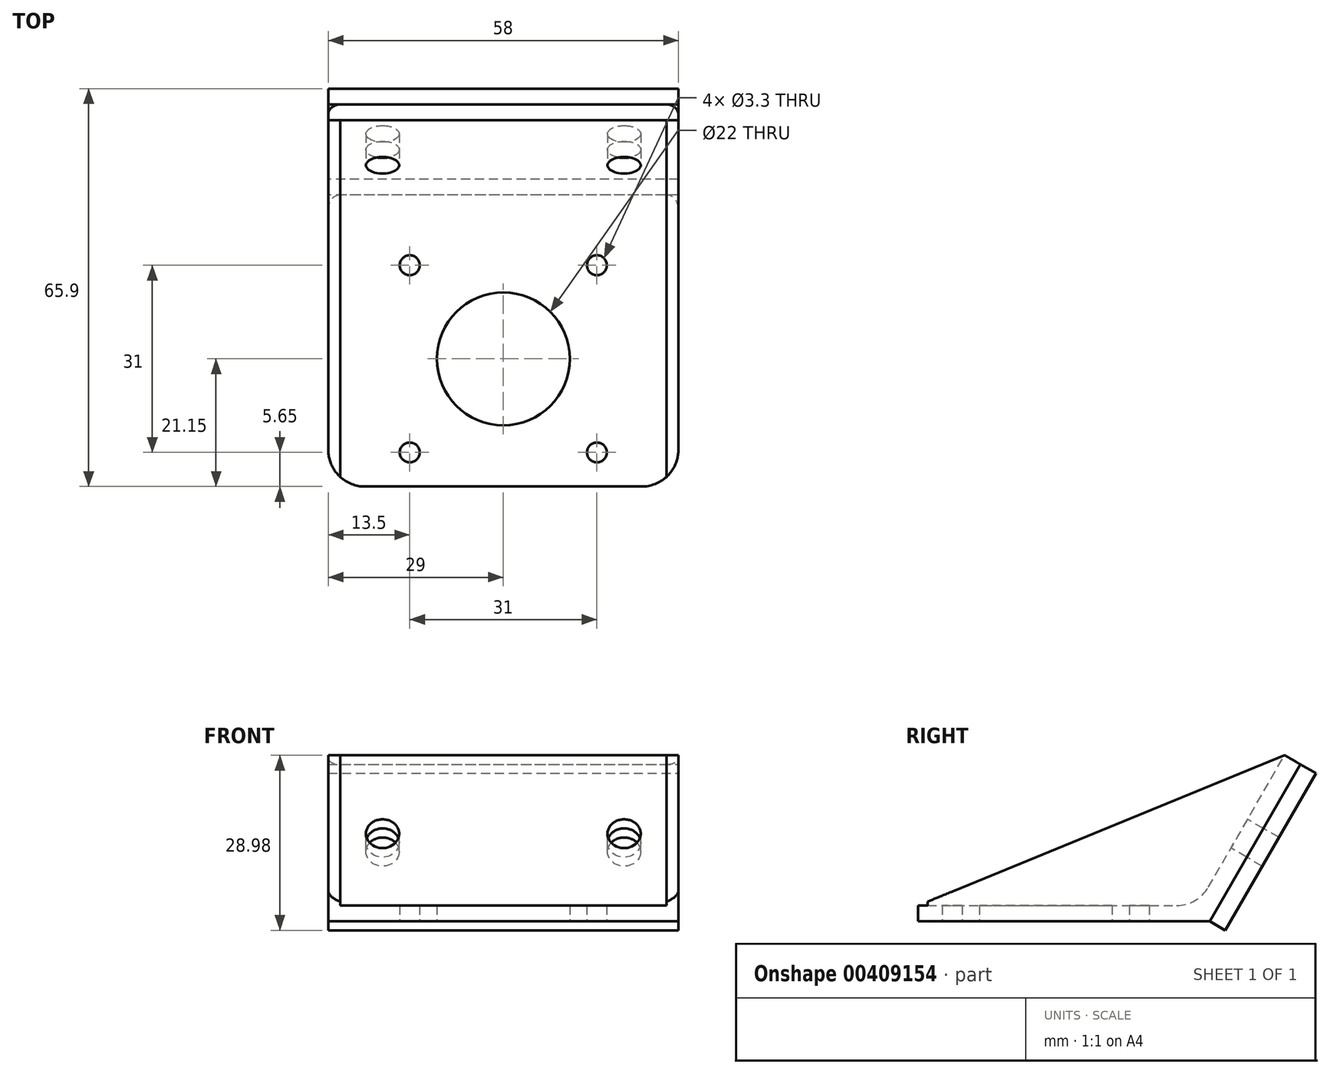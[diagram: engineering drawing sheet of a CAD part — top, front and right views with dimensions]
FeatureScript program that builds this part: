
annotation { "Feature Type Name" : "Feature", "Feature Type Description" : "" }
export const myFeature = defineFeature(function(context is Context, id is Id, definition is map)
    precondition{}
    {
        {
            var Q0;
            Q0=qCreatedBy(makeId("Top.planeOp"),FACE);
            var sketch = newSketch(context, id + "F0", { "sketchPlane" : qUnion([Q0])});
            skLineSegment(sketch, "E0.bottom", {"start": v(-21.15, 21.15) * mm, "end": v(21.15, 21.15) * mm, "construction": true});
            skLineSegment(sketch, "E0.top", {"start": v(-21.15, -21.15) * mm, "end": v(21.15, -21.15) * mm, "construction": true});
            skLineSegment(sketch, "E0.left", {"start": v(-21.15, 21.15) * mm, "end": v(-21.15, -21.15) * mm, "construction": true});
            skLineSegment(sketch, "E0.right", {"start": v(21.15, 21.15) * mm, "end": v(21.15, -21.15) * mm, "construction": true});
            skPoint(sketch, "E0.middle", {"position": v(0, 0) * mm});
            skLineSegment(sketch, "E1.bottom", {"start": v(15.5, -15.5) * mm, "end": v(-15.5, -15.5) * mm, "construction": true});
            skLineSegment(sketch, "E1.top", {"start": v(15.5, 15.5) * mm, "end": v(-15.5, 15.5) * mm, "construction": true});
            skLineSegment(sketch, "E1.left", {"start": v(15.5, -15.5) * mm, "end": v(15.5, 15.5) * mm, "construction": true});
            skLineSegment(sketch, "E1.right", {"start": v(-15.5, -15.5) * mm, "end": v(-15.5, 15.5) * mm, "construction": true});
            skCircle(sketch, "E2", {"center": v(-15.5, 15.5) * mm, "radius": 1.65 * mm});
            skCircle(sketch, "E3", {"center": v(15.5, 15.5) * mm, "radius": 1.65 * mm});
            skCircle(sketch, "E4", {"center": v(-15.5, -15.5) * mm, "radius": 1.65 * mm});
            skCircle(sketch, "E5", {"center": v(15.5, -15.5) * mm, "radius": 1.65 * mm});
            skCircle(sketch, "E6", {"center": v(0, 0) * mm, "radius": 11 * mm});
            skPoint(sketch, "E7.startSnap0", {"position": v(-21.15, 0) * mm});
            skLineSegment(sketch, "E8", {"start": v(0, 21.15) * mm, "end": v(0, -21.15) * mm, "construction": true});
            skLineSegment(sketch, "E9.bottom", {"start": v(29, -21.15) * mm, "end": v(-29, -21.15) * mm});
            skLineSegment(sketch, "E9.top", {"start": v(29, 27.15) * mm, "end": v(-29, 27.15) * mm});
            skLineSegment(sketch, "E9.left", {"start": v(29, -21.15) * mm, "end": v(29, 27.15) * mm});
            skLineSegment(sketch, "E9.right", {"start": v(-29, -21.15) * mm, "end": v(-29, 27.15) * mm});
            skPoint(sketch, "E9.middle", {"position": v(0, 3) * mm});
            skSolve(sketch);
        }
        {
            var Q0;
            Q0=makeQuery(id+"F0.imprint","IMPRINT",FACE,{"disambiguationData":[TD([[makeQuery(id+"F0.imprint","IMPRINT",EDGE,{"derivedFrom":sQuery(id+"F0.wireOp",EDGE,"E2")}),-1.0]])]});
            extrude(context, id + "F1", {"entities" : qUnion([Q0]), "depth" : 2.6 * mm, "offsetDistance" : 25 * mm});
        }
        {
            var Q0;
            Q0=makeQuery(id+"F1.opExtrude","SWEPT_FACE",FACE,{"disambiguationData":[OSD([sQuery(id+"F0.wireOp",EDGE,"E9.top")])]});
            var sketch = newSketch(context, id + "F2", { "sketchPlane" : qUnion([Q0])});
            skLineSegment(sketch, "E10.bottom", {"start": v(29, 0) * mm, "end": v(-29, 0) * mm});
            skLineSegment(sketch, "E10.top", {"start": v(29, 30) * mm, "end": v(-29, 30) * mm});
            skLineSegment(sketch, "E10.left", {"start": v(29, 0) * mm, "end": v(29, 30) * mm});
            skLineSegment(sketch, "E10.right", {"start": v(-29, 0) * mm, "end": v(-29, 30) * mm});
            skPoint(sketch, "E10.middle", {"position": v(0, 15) * mm});
            skCircle(sketch, "E11", {"center": v(20, 15) * mm, "radius": 2.75 * mm});
            skLineSegment(sketch, "E12", {"start": v(29, 15) * mm, "end": v(-29, 15) * mm, "construction": true});
            skCircle(sketch, "E13.MirrorC", {"center": v(-20, 15) * mm, "radius": 2.75 * mm});
            skCircle(sketch, "E14", {"center": v(0, 15) * mm, "radius": 2.75 * mm, "construction": true});
            skSolve(sketch);
        }
        {
            var Q0;
            {var subQ2=sQuery(id+"F2.wireOp",EDGE,"E10.top");Q0=makeQuery(id+"F2.imprint","IMPRINT",FACE,{"disambiguationData":[TD([[makeQuery(id+"F2.imprint","IMPRINT",EDGE,{"derivedFrom":subQ2}),1.0]])]});}
            var Q1;
            {var subQ0=sQuery(id+"F2.wireOp",EDGE,"E10.bottom");Q1=makeQuery(id+"F2.imprint","IMPRINT",FACE,{"disambiguationData":[TD([[makeQuery(id+"F2.imprint","IMPRINT",EDGE,{"derivedFrom":subQ0}),1.0]])]});}
            extrude(context, id + "F3", {"entities" : qUnion([Q0, Q1]), "depth" : 3 * mm, "offsetDistance" : 25 * mm});
        }
        {
            var Q0;
            Q0=makeQuery(id+"F3.opExtrude","SWEPT_BODY",BODY,{"disambiguationData":[OSD([sQuery(id+"F2.wireOp",EDGE,"E10.bottom"),sQuery(id+"F2.wireOp",EDGE,"E10.top"),sQuery(id+"F2.wireOp",EDGE,"E10.left"),sQuery(id+"F2.wireOp",EDGE,"E10.right"),sQuery(id+"F2.wireOp",EDGE,"E11"),sQuery(id+"F2.wireOp",EDGE,"E13.MirrorC")])]});
            var Q1;
            Q1=makeQuery(id+"F3.opExtrude","CAP_EDGE",EDGE,{"disambiguationData":[OSD([sQuery(id+"F2.wireOp",EDGE,"E10.bottom")])],"isStart":false});
            transform(context, id + "F4", {"entities" : qUnion([Q0]), "transformType" : TransformType.ROTATION, "transformAxis" : qUnion([Q1]), "angle" : 30 * degree, "makeCopy" : false});
        }
        {
            var Q0;
            Q0=makeQuery(id+"F3.opExtrude","SWEPT_BODY",BODY,{"disambiguationData":[OSD([sQuery(id+"F2.wireOp",EDGE,"E10.bottom"),sQuery(id+"F2.wireOp",EDGE,"E10.top"),sQuery(id+"F2.wireOp",EDGE,"E10.left"),sQuery(id+"F2.wireOp",EDGE,"E10.right"),sQuery(id+"F2.wireOp",EDGE,"E11"),sQuery(id+"F2.wireOp",EDGE,"E13.MirrorC")])]});
            var Q1;
            Q1=makeQuery(id+"F3.opExtrude","CAP_VERTEX",VERTEX,{"disambiguationData":[OSD([sQuery(id+"F2.wireOp",EDGE,"E10.bottom"),sQuery(id+"F2.wireOp",EDGE,"E10.left")])],"isStart":false});
            var Q2;
            Q2=makeQuery(id+"F1.opExtrude","CAP_VERTEX",VERTEX,{"disambiguationData":[OSD([sQuery(id+"F0.wireOp",EDGE,"E9.top"),sQuery(id+"F0.wireOp",EDGE,"E9.right")])],"isStart":true});
            transform(context, id + "F5", {"entities" : qUnion([Q0]), "transformType" : TransformType.TRANSLATION_ENTITY, "oppositeDirectionEntity" : false, "transformLine" : qUnion([Q1, Q2]), "makeCopy" : false});
        }
        {
            var Q0;
            Q0=makeQuery(id+"F1.opExtrude","SWEPT_BODY",BODY,{"disambiguationData":[OSD([sQuery(id+"F0.wireOp",EDGE,"E2"),sQuery(id+"F0.wireOp",EDGE,"E3"),sQuery(id+"F0.wireOp",EDGE,"E4"),sQuery(id+"F0.wireOp",EDGE,"E5"),sQuery(id+"F0.wireOp",EDGE,"E6"),sQuery(id+"F0.wireOp",EDGE,"E9.bottom"),sQuery(id+"F0.wireOp",EDGE,"E9.top"),sQuery(id+"F0.wireOp",EDGE,"E9.left"),sQuery(id+"F0.wireOp",EDGE,"E9.right")])]});
            var Q1;
            Q1=makeQuery(id+"F3.opExtrude","SWEPT_BODY",BODY,{"disambiguationData":[OSD([sQuery(id+"F2.wireOp",EDGE,"E10.bottom"),sQuery(id+"F2.wireOp",EDGE,"E10.top"),sQuery(id+"F2.wireOp",EDGE,"E10.left"),sQuery(id+"F2.wireOp",EDGE,"E10.right"),sQuery(id+"F2.wireOp",EDGE,"E11"),sQuery(id+"F2.wireOp",EDGE,"E13.MirrorC")])]});
            booleanBodies(context, id + "F6", {"operationType" : BooleanOperationType.UNION, "tools" : qUnion([Q0, Q1])});
        }
        {
            var Q0;
            Q0=makeQuery(id+"F3.opExtrude","CAP_FACE",FACE,{"disambiguationData":[OSD([sQuery(id+"F2.wireOp",EDGE,"E10.bottom"),sQuery(id+"F2.wireOp",EDGE,"E10.top"),sQuery(id+"F2.wireOp",EDGE,"E10.left"),sQuery(id+"F2.wireOp",EDGE,"E10.right"),sQuery(id+"F2.wireOp",EDGE,"E11"),sQuery(id+"F2.wireOp",EDGE,"E13.MirrorC")])],"isStart":false});
            extrude(context, id + "F7", {"entities" : qUnion([Q0]), "depth" : 3 * mm, "offsetDistance" : 25 * mm});
        }
        {
            var Q0;
            Q0=makeQuery(id+"F3.boolean.opBoolean","MERGE",FACE,{"derivedFrom":[makeQuery(id+"F1.opExtrude","SWEPT_FACE",FACE,{"disambiguationData":[OSD([sQuery(id+"F0.wireOp",EDGE,"E9.right")])]}),makeQuery(id+"F3.opExtrude","SWEPT_FACE",FACE,{"disambiguationData":[OSD([sQuery(id+"F2.wireOp",EDGE,"E10.left")])]})]});
            var sketch = newSketch(context, id + "F8", { "sketchPlane" : qUnion([Q0])});
            skLineSegment(sketch, "E15", {"start": v(-39.55, 27.48) * mm, "end": v(21.15, 2.6) * mm});
            skSolve(sketch);
        }
        {
            var Q0;
            Q0=makeQuery(id+"F8.imprint","IMPRINT",FACE,{"disambiguationData":[TD([[makeQuery(id+"F8.imprint","IMPRINT",EDGE,{"derivedFrom":sQuery(id+"F8.wireOp",EDGE,"E15")}),-1.0]])]});
            extrude(context, id + "F9", {"entities" : qUnion([Q0]), "operationType" : NewBodyOperationType.ADD, "oppositeDirection" : true, "depth" : 2 * mm, "offsetDistance" : 25 * mm});
        }
        {
            var Q0;
            Q0=makeQuery(id+"F3.boolean.opBoolean","MERGE",FACE,{"derivedFrom":[makeQuery(id+"F1.opExtrude","SWEPT_FACE",FACE,{"disambiguationData":[OSD([sQuery(id+"F0.wireOp",EDGE,"E9.left")])]}),makeQuery(id+"F3.opExtrude","SWEPT_FACE",FACE,{"disambiguationData":[OSD([sQuery(id+"F2.wireOp",EDGE,"E10.right")])]})]});
            var sketch = newSketch(context, id + "F10", { "sketchPlane" : qUnion([Q0])});
            skLineSegment(sketch, "E16", {"start": v(39.55, 27.48) * mm, "end": v(-21.15, 2.6) * mm});
            skSolve(sketch);
        }
        {
            var Q0;
            Q0=makeQuery(id+"F10.imprint","IMPRINT",FACE,{"disambiguationData":[TD([[makeQuery(id+"F10.imprint","IMPRINT",EDGE,{"derivedFrom":sQuery(id+"F10.wireOp",EDGE,"E16")}),1.0]])]});
            extrude(context, id + "F11", {"entities" : qUnion([Q0]), "operationType" : NewBodyOperationType.ADD, "oppositeDirection" : true, "depth" : 2 * mm, "offsetDistance" : 25 * mm});
        }
        {
            var Q0;
            Q0=makeQuery(id+"F3.opExtrude","CAP_FACE",FACE,{"disambiguationData":[OSD([sQuery(id+"F2.wireOp",EDGE,"E10.bottom"),sQuery(id+"F2.wireOp",EDGE,"E10.top"),sQuery(id+"F2.wireOp",EDGE,"E10.left"),sQuery(id+"F2.wireOp",EDGE,"E10.right"),sQuery(id+"F2.wireOp",EDGE,"E11"),sQuery(id+"F2.wireOp",EDGE,"E13.MirrorC"),sQuery(id+"F2.wireOp",EDGE,"E14")])],"isStart":true});
            var sketch = newSketch(context, id + "F12", { "sketchPlane" : qUnion([Q0])});
            skCircle(sketch, "E17", {"center": v(-20, 28.57) * mm, "radius": 6 * mm});
            skCircle(sketch, "E18", {"center": v(20, 28.57) * mm, "radius": 6 * mm});
            skSolve(sketch);
        }
        {
            var Q0;
            Q0=makeQuery(id+"F1.opExtrude","CAP_EDGE",EDGE,{"disambiguationData":[OSD([sQuery(id+"F0.wireOp",EDGE,"E9.top")])],"isStart":false});
            var Q1;
            Q1=makeQuery(id+"F1.opExtrude","SWEPT_EDGE",EDGE,{"disambiguationData":[OSD([sQuery(id+"F0.wireOp",EDGE,"E9.bottom"),sQuery(id+"F0.wireOp",EDGE,"E9.right")])]});
            var Q2;
            Q2=makeQuery(id+"F1.opExtrude","SWEPT_EDGE",EDGE,{"disambiguationData":[OSD([sQuery(id+"F0.wireOp",EDGE,"E9.bottom"),sQuery(id+"F0.wireOp",EDGE,"E9.left")])]});
            var Q3;
            Q3=makeQuery(id+"F6.opBoolean","INTERSECT",EDGE,{"derivedFrom":[makeQuery(id+"F1.opExtrude","CAP_FACE",FACE,{"disambiguationData":[OSD([sQuery(id+"F0.wireOp",EDGE,"E2"),sQuery(id+"F0.wireOp",EDGE,"E3"),sQuery(id+"F0.wireOp",EDGE,"E4"),sQuery(id+"F0.wireOp",EDGE,"E5"),sQuery(id+"F0.wireOp",EDGE,"E6"),sQuery(id+"F0.wireOp",EDGE,"E9.bottom"),sQuery(id+"F0.wireOp",EDGE,"E9.top"),sQuery(id+"F0.wireOp",EDGE,"E9.left"),sQuery(id+"F0.wireOp",EDGE,"E9.right")])],"isStart":false}),makeQuery(id+"F3.opExtrude","CAP_FACE",FACE,{"disambiguationData":[OSD([sQuery(id+"F2.wireOp",EDGE,"E10.bottom"),sQuery(id+"F2.wireOp",EDGE,"E10.top"),sQuery(id+"F2.wireOp",EDGE,"E10.left"),sQuery(id+"F2.wireOp",EDGE,"E10.right"),sQuery(id+"F2.wireOp",EDGE,"E11"),sQuery(id+"F2.wireOp",EDGE,"E13.MirrorC")])],"isStart":true})]});
            fillet(context, id + "F13", {"entities" : qUnion([Q0, Q1, Q2, Q3]), "radius" : 6.1 * mm, "allowEdgeOverflow" : false});
        }
        {
            var Q0;
            Q0=makeQuery(id+"F3.opExtrude","CAP_EDGE",EDGE,{"disambiguationData":[OSD([sQuery(id+"F2.wireOp",EDGE,"E10.right")])],"isStart":false});
            var Q1;
            Q1=makeQuery(id+"F3.opExtrude","CAP_EDGE",EDGE,{"disambiguationData":[OSD([sQuery(id+"F2.wireOp",EDGE,"E10.left")])],"isStart":false});
            var Q2;
            Q2=makeQuery(id+"F11.opExtrude","CAP_EDGE",EDGE,{"disambiguationData":[OSD([sQuery(id+"F2.wireOp",EDGE,"E10.right")])],"isStart":false});
            var Q3;
            Q3=makeQuery(id+"F9.opExtrude","CAP_EDGE",EDGE,{"disambiguationData":[OSD([sQuery(id+"F2.wireOp",EDGE,"E10.left")])],"isStart":false});
            fillet(context, id + "F14", {"entities" : qUnion([Q0, Q1, Q2, Q3]), "radius" : 2 * mm, "tangentPropagation" : true, "allowEdgeOverflow" : false});
        }
        {
            var Q0;
            Q0=makeQuery(id+"F12.imprint","IMPRINT",FACE,{"disambiguationData":[TD([[makeQuery(id+"F12.imprint","IMPRINT",EDGE,{"derivedFrom":sQuery(id+"F12.wireOp",EDGE,"E17")}),1.0]])]});
            var Q1;
            Q1=makeQuery(id+"F12.imprint","IMPRINT",FACE,{"disambiguationData":[TD([[makeQuery(id+"F12.imprint","IMPRINT",EDGE,{"derivedFrom":sQuery(id+"F12.wireOp",EDGE,"E18")}),1.0]])]});
            extrude(context, id + "F15", {"entities" : qUnion([Q0, Q1]), "operationType" : NewBodyOperationType.REMOVE, "depth" : 25 * mm, "offsetDistance" : 25 * mm});
        }
    });
